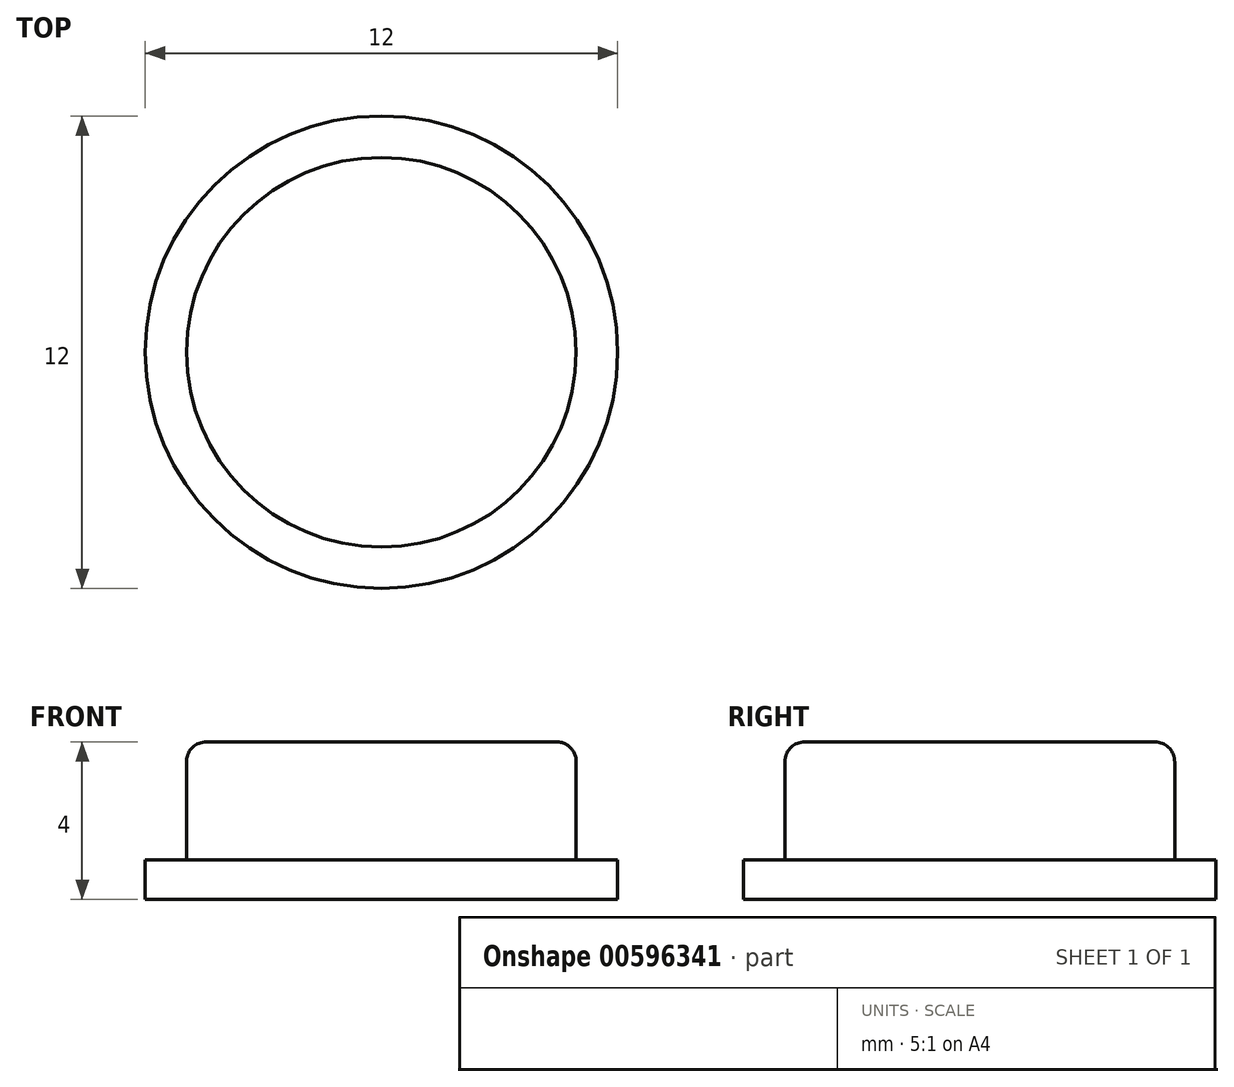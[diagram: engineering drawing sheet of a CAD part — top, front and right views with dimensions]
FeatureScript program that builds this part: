
annotation { "Feature Type Name" : "Feature", "Feature Type Description" : "" }
export const myFeature = defineFeature(function(context is Context, id is Id, definition is map)
    precondition{}
    {
        {
            var Q0;
            Q0=qCreatedBy(makeId("Top.planeOp"),FACE);
            var sketch = newSketch(context, id + "F0", { "sketchPlane" : qUnion([Q0])});
            skCircle(sketch, "E0", {"center": v(-42.84, 43.44) * mm, "radius": 6 * mm});
            skCircle(sketch, "E1", {"center": v(-42.84, 43.44) * mm, "radius": 4.95 * mm});
            skSolve(sketch);
        }
        {
            var Q0;
            Q0=makeQuery(id+"F0.imprint","IMPRINT",FACE,{"disambiguationData":[TD([[makeQuery(id+"F0.imprint","IMPRINT",EDGE,{"derivedFrom":sQuery(id+"F0.wireOp",EDGE,"E1")}),1.0]])]});
            extrude(context, id + "F1", {"entities" : qUnion([Q0]), "depth" : 4 * mm, "offsetDistance" : 25 * mm});
        }
        {
            var Q0;
            Q0=makeQuery(id+"F1.opExtrude","CAP_FACE",FACE,{"disambiguationData":[OSD([sQuery(id+"F0.wireOp",EDGE,"E1")])],"isStart":true});
            var sketch = newSketch(context, id + "F2", { "sketchPlane" : qUnion([Q0])});
            skCircle(sketch, "E2", {"center": v(-42.84, -43.44) * mm, "radius": 6 * mm});
            skSolve(sketch);
        }
        {
            var Q0;
            Q0=makeQuery(id+"F2.imprint","IMPRINT",FACE,{"disambiguationData":[TD([[makeQuery(id+"F2.imprint","IMPRINT",EDGE,{"derivedFrom":sQuery(id+"F2.wireOp",EDGE,"E2")}),1.0]])]});
            extrude(context, id + "F3", {"entities" : qUnion([Q0]), "operationType" : NewBodyOperationType.ADD, "oppositeDirection" : true, "depth" : 1 * mm, "offsetDistance" : 25 * mm});
        }
        {
            var Q0;
            Q0=makeQuery(id+"F1.opExtrude","CAP_EDGE",EDGE,{"disambiguationData":[OSD([sQuery(id+"F0.wireOp",EDGE,"E1")])],"isStart":false});
            fillet(context, id + "F4", {"entities" : qUnion([Q0]), "radius" : 0.5 * mm, "tangentPropagation" : true, "allowEdgeOverflow" : false});
        }
    });
